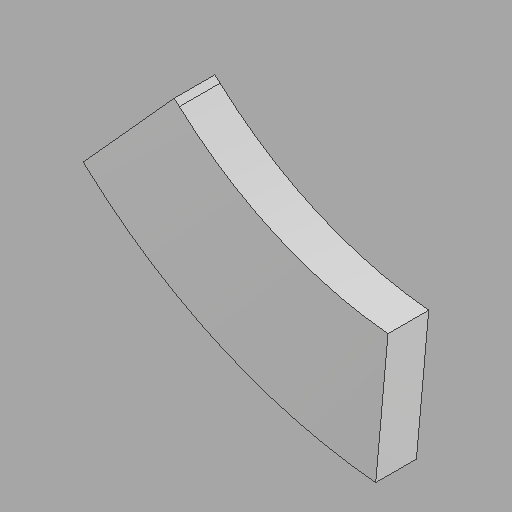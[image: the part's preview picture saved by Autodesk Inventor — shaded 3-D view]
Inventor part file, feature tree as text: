
AUTODESK INVENTOR PART (.ipt)
format: ipt  version: 2022.1 (Build 261234020, 234B)  size: 90,624 bytes
history: imported  units: in
note: dims shown in document units (in); Inventor stores cm internally (conversion verified against a paired STEP export)
features: imported_body x1
ambient origin geometry x8: Origin, YZ Plane, XZ Plane, XY Plane, X Axis, Y Axis, Z Axis, Center Point
bodies: Solid1 (imported_parasolid), Body1 (imported_parasolid)
feature tree (1):
  imported_body  NMx_Import_Brep_tag  [imported B-rep: ~8 faces, bbox_mm=[1140.794019, 868.777686, 152.4]]
